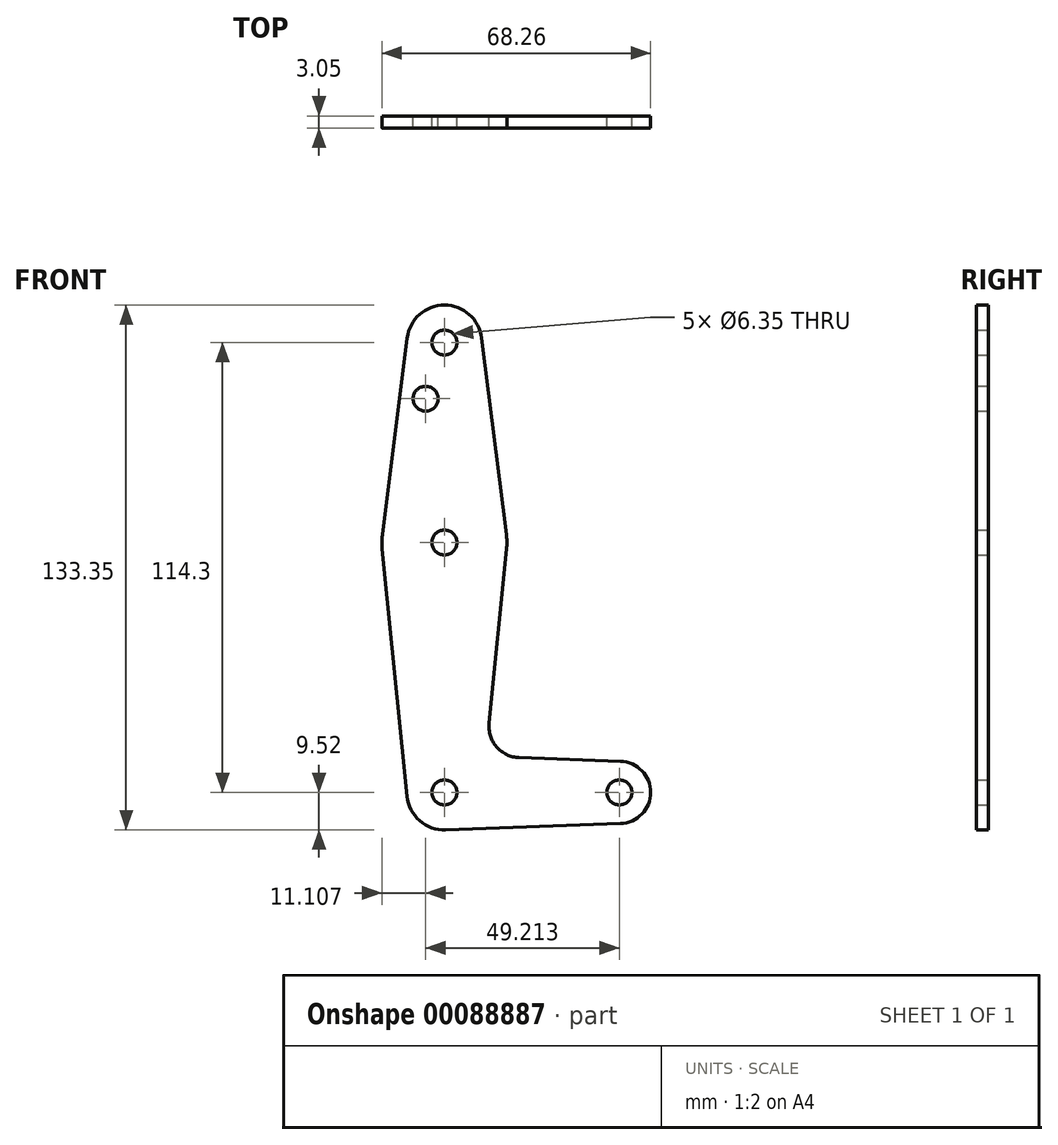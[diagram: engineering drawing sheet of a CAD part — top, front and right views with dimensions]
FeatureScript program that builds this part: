
annotation { "Feature Type Name" : "Feature", "Feature Type Description" : "" }
export const myFeature = defineFeature(function(context is Context, id is Id, definition is map)
    precondition{}
    {
        {
            var Q0;
            Q0=qCreatedBy(makeId("Front.planeOp"),FACE);
            var sketch = newSketch(context, id + "F0", { "sketchPlane" : qUnion([Q0])});
            skCircle(sketch, "E0", {"center": v(0, 0) * mm, "radius": 9.53 * mm});
            skCircle(sketch, "E1", {"center": v(0, 63.5) * mm, "radius": 15.88 * mm});
            skCircle(sketch, "E2", {"center": v(0, 114.3) * mm, "radius": 9.53 * mm});
            skCircle(sketch, "E3", {"center": v(44.45, 0) * mm, "radius": 7.94 * mm});
            skLineSegment(sketch, "E4", {"start": v(0, 114.3) * mm, "end": v(0, 0) * mm, "construction": true});
            skLineSegment(sketch, "E5", {"start": v(0, 0) * mm, "end": v(44.45, 0) * mm, "construction": true});
            skLineSegment(sketch, "E6", {"start": v(-15.75, 65.48) * mm, "end": v(-9.45, 115.5) * mm});
            skLineSegment(sketch, "E7", {"start": v(9.45, 115.5) * mm, "end": v(15.75, 65.48) * mm});
            skLineSegment(sketch, "E8", {"start": v(0.34, -9.52) * mm, "end": v(44.73, -7.93) * mm});
            skCircle(sketch, "E9", {"center": v(0, 114.3) * mm, "radius": 3.18 * mm});
            skCircle(sketch, "E10", {"center": v(0, 63.5) * mm, "radius": 3.18 * mm});
            skCircle(sketch, "E11", {"center": v(0, 0) * mm, "radius": 3.18 * mm});
            skCircle(sketch, "E12", {"center": v(44.45, 0) * mm, "radius": 3.18 * mm});
            skCircle(sketch, "E13", {"center": v(-4.76, 100.03) * mm, "radius": 3.18 * mm});
            skLineSegment(sketch, "E14", {"start": v(15.8, 61.91) * mm, "end": v(11.34, 17.6) * mm});
            skLineSegment(sketch, "E15", {"start": v(18.97, 8.85) * mm, "end": v(44.73, 7.93) * mm});
            skLineSegment(sketch, "E16", {"start": v(-15.8, 61.91) * mm, "end": v(-9.48, -0.95) * mm});
            skArc(sketch, "E17.filletArc", {"start": v(11.34, 17.6) * mm, "mid": v(13.26, 11.57) * mm, "end": v(18.97, 8.85) * mm});
            skSolve(sketch);
        }
        {
            var Q0;
            Q0 = qSketchRegion(id + "F0", true);
            extrude(context, id + "F1", {"entities" : qUnion([Q0]), "depth" : 3.05 * mm});
        }
        {
            var Q0;
            Q0 = qSketchRegion(id + "F0", true);
            extrude(context, id + "F2", {"entities" : qUnion([Q0]), "operationType" : NewBodyOperationType.ADD, "depth" : 3.05 * mm});
        }
    });
